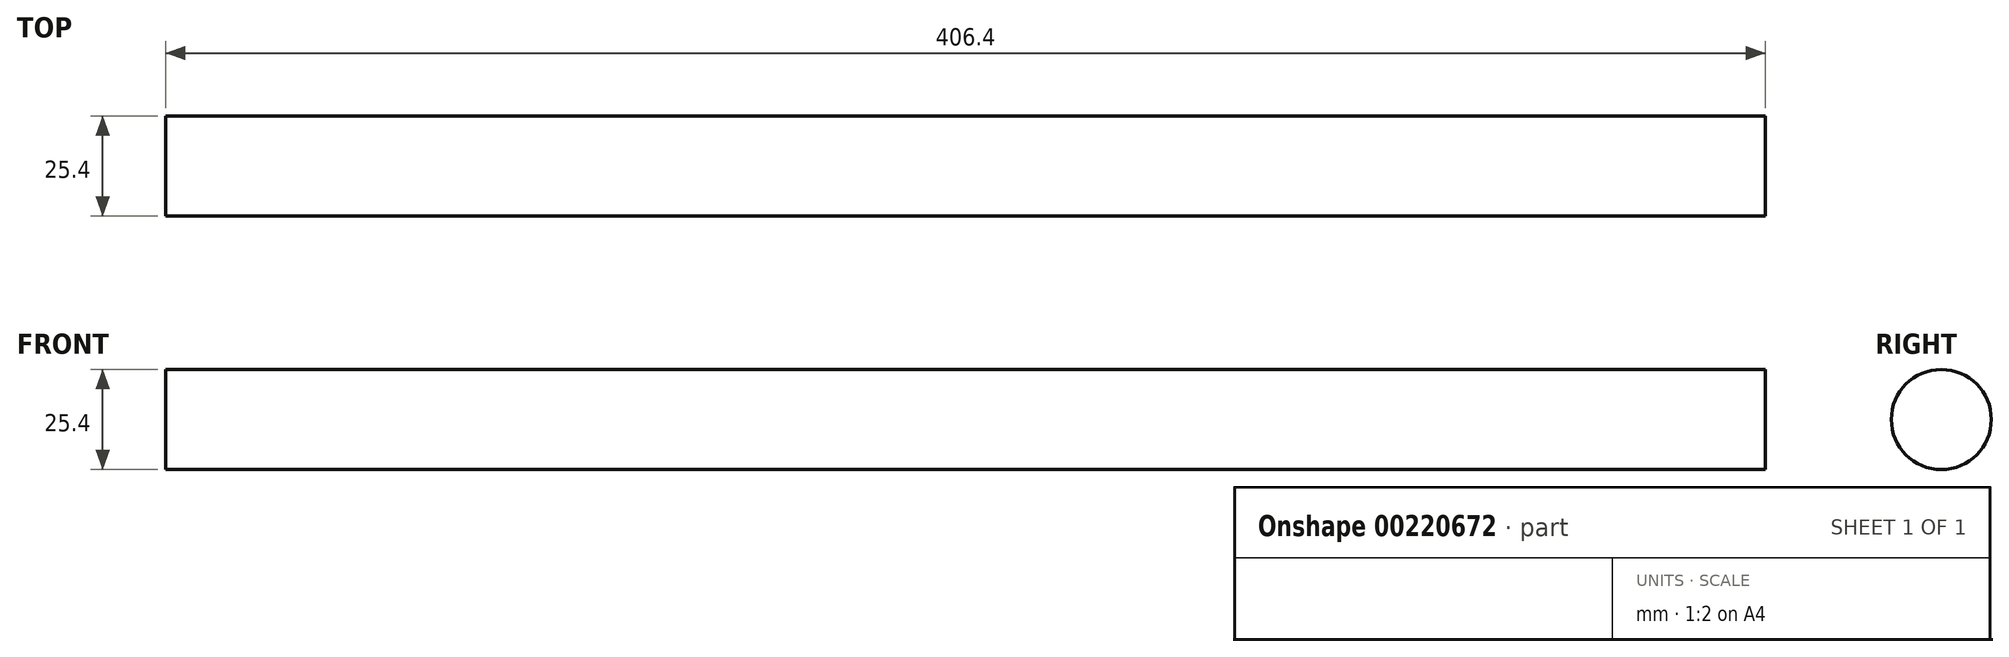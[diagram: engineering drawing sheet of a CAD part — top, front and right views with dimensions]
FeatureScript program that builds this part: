
annotation { "Feature Type Name" : "Feature", "Feature Type Description" : "" }
export const myFeature = defineFeature(function(context is Context, id is Id, definition is map)
    precondition{}
    {
        {
            var Q0;
            Q0=qCreatedBy(makeId("Front.planeOp"),FACE);
            var sketch = newSketch(context, id + "F0", { "sketchPlane" : qUnion([Q0])});
            skLineSegment(sketch, "E0.bottom", {"start": v(0, 25.4) * mm, "end": v(406.4, 25.4) * mm});
            skLineSegment(sketch, "E0.top", {"start": v(0, 0) * mm, "end": v(406.4, 0) * mm});
            skLineSegment(sketch, "E0.left", {"start": v(0, 25.4) * mm, "end": v(0, 0) * mm});
            skLineSegment(sketch, "E0.right", {"start": v(406.4, 25.4) * mm, "end": v(406.4, 0) * mm});
            skSolve(sketch);
        }
        {
            var Q0;
            Q0=makeQuery(id+"F0.imprint","IMPRINT",FACE,{"disambiguationData":[TD([[makeQuery(id+"F0.imprint","IMPRINT",EDGE,{"derivedFrom":sQuery(id+"F0.wireOp",EDGE,"E0.bottom")}),-1.0]])]});
            extrude(context, id + "F1", {"entities" : qUnion([Q0]), "endBound" : BoundingType.SYMMETRIC, "depth" : 25.4 * mm});
        }
        {
            var Q0;
            Q0=makeQuery(id+"F1.opExtrude","CAP_EDGE",EDGE,{"disambiguationData":[OSD([sQuery(id+"F0.wireOp",EDGE,"E0.top")])],"isStart":false});
            var Q1;
            Q1=makeQuery(id+"F1.opExtrude","CAP_EDGE",EDGE,{"disambiguationData":[OSD([sQuery(id+"F0.wireOp",EDGE,"E0.bottom")])],"isStart":false});
            var Q2;
            Q2=makeQuery(id+"F1.opExtrude","CAP_EDGE",EDGE,{"disambiguationData":[OSD([sQuery(id+"F0.wireOp",EDGE,"E0.bottom")])],"isStart":true});
            var Q3;
            Q3=makeQuery(id+"F1.opExtrude","CAP_EDGE",EDGE,{"disambiguationData":[OSD([sQuery(id+"F0.wireOp",EDGE,"E0.top")])],"isStart":true});
            fillet(context, id + "F2", {"entities" : qUnion([Q0, Q1, Q2, Q3]), "radius" : 12.7 * mm, "tangentPropagation" : true, "allowEdgeOverflow" : false});
        }
    });
